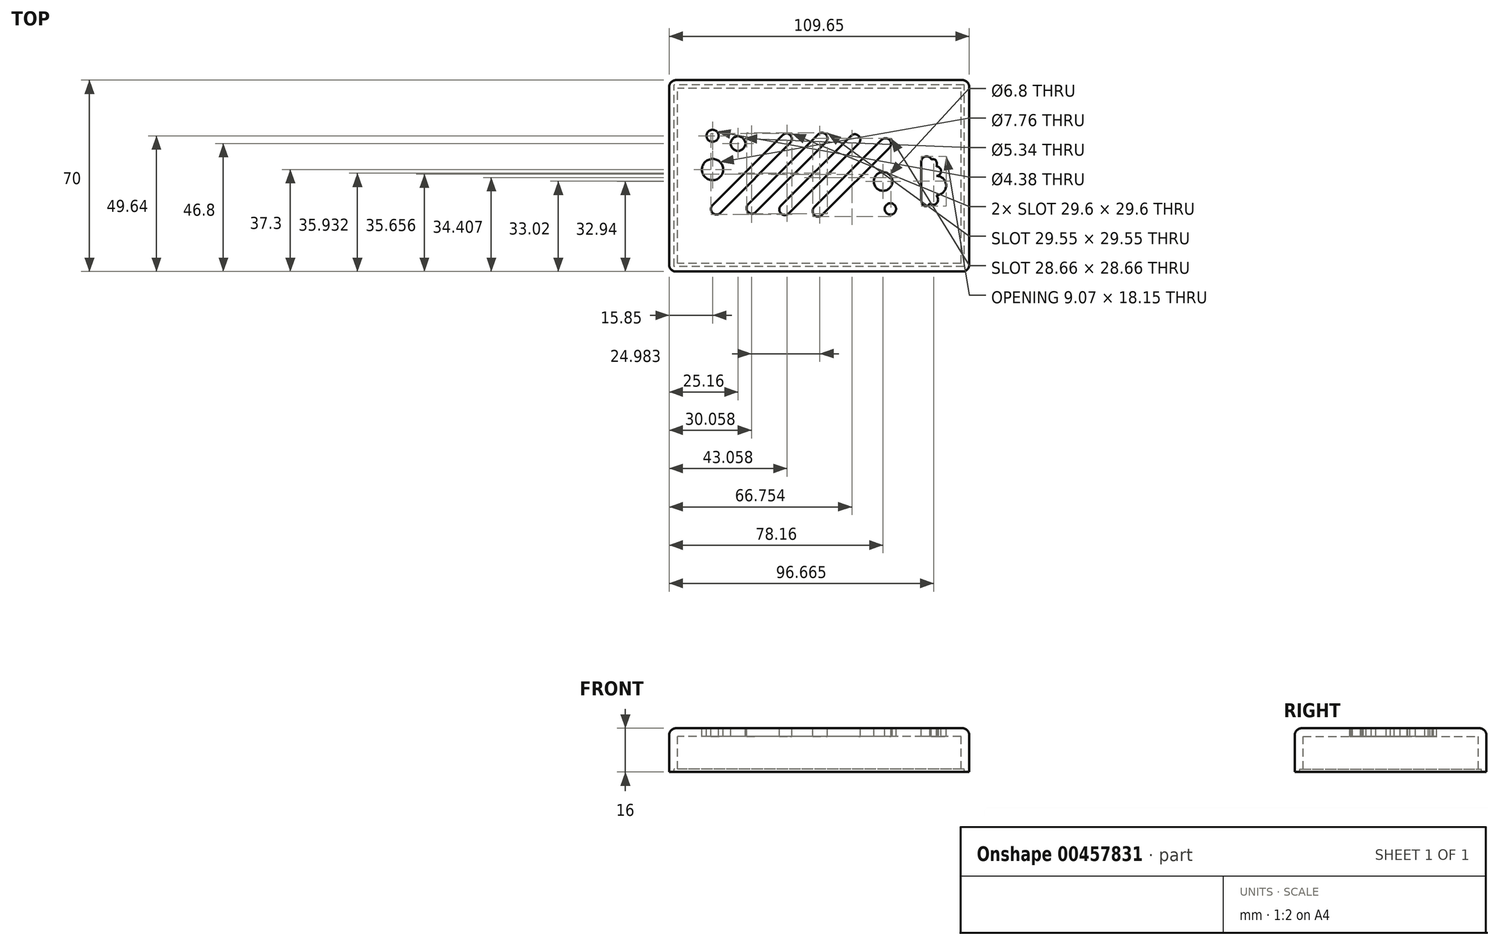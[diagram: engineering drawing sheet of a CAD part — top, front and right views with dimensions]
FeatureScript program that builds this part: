
annotation { "Feature Type Name" : "Feature", "Feature Type Description" : "" }
export const myFeature = defineFeature(function(context is Context, id is Id, definition is map)
    precondition{}
    {
        {
            var Q0;
            Q0=qCreatedBy(makeId("Top.planeOp"),FACE);
            var sketch = newSketch(context, id + "F0", { "sketchPlane" : qUnion([Q0])});
            skLineSegment(sketch, "E0.0", {"start": v(57.26, 37.06) * mm, "end": v(51.26, 37.06) * mm});
            skLineSegment(sketch, "E0.1", {"start": v(57.26, -32.94) * mm, "end": v(57.26, 37.06) * mm});
            skLineSegment(sketch, "E0.2", {"start": v(57.26, -32.94) * mm, "end": v(-24.39, -32.94) * mm});
            skLineSegment(sketch, "E0.3", {"start": v(-52.39, -32.94) * mm, "end": v(-52.39, 37.06) * mm});
            skLineSegment(sketch, "E1", {"start": v(-24.39, -32.94) * mm, "end": v(-46.39, -32.94) * mm});
            skLineSegment(sketch, "E2", {"start": v(-46.39, -32.94) * mm, "end": v(-52.39, -32.94) * mm});
            skLineSegment(sketch, "E3", {"start": v(51.26, 37.06) * mm, "end": v(29.26, 37.06) * mm});
            skLineSegment(sketch, "E4", {"start": v(29.26, 37.06) * mm, "end": v(-52.39, 37.06) * mm});
            skSolve(sketch);
        }
        {
            var Q0;
            Q0=makeQuery(id+"F0.imprint","IMPRINT",FACE,{"disambiguationData":[TD([[makeQuery(id+"F0.imprint","IMPRINT",EDGE,{"derivedFrom":sQuery(id+"F0.wireOp",EDGE,"E0.0")}),1.0]])]});
            extrude(context, id + "F1", {"entities" : qUnion([Q0]), "oppositeDirection" : true, "depth" : 15 * mm});
        }
        {
            var Q0;
            Q0=makeQuery(id+"F1.opExtrude","CAP_FACE",FACE,{"disambiguationData":[OSD([sQuery(id+"F0.wireOp",EDGE,"E0.0"),sQuery(id+"F0.wireOp",EDGE,"E0.1"),sQuery(id+"F0.wireOp",EDGE,"E0.2"),sQuery(id+"F0.wireOp",EDGE,"E0.3"),sQuery(id+"F0.wireOp",EDGE,"E1"),sQuery(id+"F0.wireOp",EDGE,"E2"),sQuery(id+"F0.wireOp",EDGE,"E3"),sQuery(id+"F0.wireOp",EDGE,"E4")])],"isStart":false});
            shell(context, id + "F2", {"entities" : qUnion([Q0]), "thickness" : 3 * mm});
        }
        {
            var Q0;
            Q0=makeQuery(id+"F1.opExtrude","SWEPT_EDGE",EDGE,{"disambiguationData":[OSD([sQuery(id+"F0.wireOp",EDGE,"E0.1"),sQuery(id+"F0.wireOp",EDGE,"E0.2")])]});
            var Q1;
            Q1=makeQuery(id+"F1.opExtrude","SWEPT_EDGE",EDGE,{"disambiguationData":[OSD([sQuery(id+"F0.wireOp",EDGE,"E0.0"),sQuery(id+"F0.wireOp",EDGE,"E0.1")])]});
            var Q2;
            Q2=makeQuery(id+"F1.opExtrude","SWEPT_EDGE",EDGE,{"disambiguationData":[OSD([sQuery(id+"F0.wireOp",EDGE,"E0.3"),sQuery(id+"F0.wireOp",EDGE,"E2")])]});
            var Q3;
            Q3=makeQuery(id+"F1.opExtrude","SWEPT_EDGE",EDGE,{"disambiguationData":[OSD([sQuery(id+"F0.wireOp",EDGE,"E0.3"),sQuery(id+"F0.wireOp",EDGE,"E4")])]});
            var Q4;
            Q4=makeQuery(id+"F1.opExtrude","CAP_EDGE",EDGE,{"disambiguationData":[OSD([sQuery(id+"F0.wireOp",EDGE,"E0.3")])],"isStart":true});
            var Q5;
            Q5=makeQuery(id+"F1.opExtrude","CAP_EDGE",EDGE,{"disambiguationData":[OSD([sQuery(id+"F0.wireOp",EDGE,"E0.2"),sQuery(id+"F0.wireOp",EDGE,"E1"),sQuery(id+"F0.wireOp",EDGE,"E2")])],"isStart":true});
            var Q6;
            Q6=makeQuery(id+"F1.opExtrude","CAP_EDGE",EDGE,{"disambiguationData":[OSD([sQuery(id+"F0.wireOp",EDGE,"E0.0"),sQuery(id+"F0.wireOp",EDGE,"E3"),sQuery(id+"F0.wireOp",EDGE,"E4")])],"isStart":true});
            var Q7;
            Q7=makeQuery(id+"F1.opExtrude","CAP_EDGE",EDGE,{"disambiguationData":[OSD([sQuery(id+"F0.wireOp",EDGE,"E0.1")])],"isStart":true});
            fillet(context, id + "F3", {"entities" : qUnion([Q0, Q1, Q2, Q3, Q4, Q5, Q6, Q7]), "radius" : 2.5 * mm, "tangentPropagation" : true, "allowEdgeOverflow" : false});
        }
        {
            var Q0;
            Q0=qCreatedBy(makeId("Top.planeOp"),FACE);
            var sketch = newSketch(context, id + "F4", { "sketchPlane" : qUnion([Q0])});
            skLineSegment(sketch, "E5.top", {"start": v(-36.54, -8.66) * mm, "end": v(-36.54, -8.66) * mm});
            skLineSegment(sketch, "E5.left", {"start": v(-10.95, 16.93) * mm, "end": v(-36.54, -8.66) * mm});
            skLineSegment(sketch, "E5.right", {"start": v(-8.12, 14.1) * mm, "end": v(-33.71, -11.5) * mm});
            skArc(sketch, "E6", {"start": v(-8.12, 14.1) * mm, "mid": v(-8.12, 16.93) * mm, "end": v(-10.95, 16.93) * mm});
            skArc(sketch, "E7", {"start": v(-36.54, -8.66) * mm, "mid": v(-36.54, -11.5) * mm, "end": v(-33.71, -11.5) * mm});
            skLineSegment(sketch, "E8.left", {"start": v(2.03, 17.18) * mm, "end": v(-23.52, -8.37) * mm});
            skLineSegment(sketch, "E8.right", {"start": v(4.85, 14.35) * mm, "end": v(-20.7, -11.2) * mm});
            skArc(sketch, "E9", {"start": v(4.85, 14.35) * mm, "mid": v(4.86, 17.18) * mm, "end": v(2.03, 17.18) * mm});
            skArc(sketch, "E10", {"start": v(-23.52, -8.37) * mm, "mid": v(-23.52, -11.2) * mm, "end": v(-20.7, -11.2) * mm});
            skLineSegment(sketch, "E11.left", {"start": v(14.03, 16.7) * mm, "end": v(-11.56, -8.9) * mm});
            skLineSegment(sketch, "E11.right", {"start": v(16.86, 13.86) * mm, "end": v(-8.73, -11.73) * mm});
            skArc(sketch, "E12", {"start": v(16.86, 13.86) * mm, "mid": v(16.86, 16.7) * mm, "end": v(14.03, 16.7) * mm});
            skArc(sketch, "E13", {"start": v(-11.56, -8.9) * mm, "mid": v(-11.56, -11.73) * mm, "end": v(-8.73, -11.73) * mm});
            skLineSegment(sketch, "E14.left", {"start": v(25.28, 15.21) * mm, "end": v(0.62, -9.45) * mm});
            skLineSegment(sketch, "E14.right", {"start": v(28.11, 12.38) * mm, "end": v(3.44, -12.28) * mm});
            skArc(sketch, "E15", {"start": v(28.11, 12.38) * mm, "mid": v(28.11, 15.21) * mm, "end": v(25.28, 15.21) * mm});
            skArc(sketch, "E16", {"start": v(0.62, -9.45) * mm, "mid": v(0.62, -12.28) * mm, "end": v(3.44, -12.28) * mm});
            skPoint(sketch, "E17.orphan", {"position": v(-8.73, 13.5) * mm});
            skSolve(sketch);
        }
        {
            var Q0;
            Q0=makeQuery(id+"F4.imprint","IMPRINT",FACE,{"disambiguationData":[TD([[makeQuery(id+"F4.imprint","IMPRINT",EDGE,{"derivedFrom":sQuery(id+"F4.wireOp",EDGE,"E14.left")}),1.0]])]});
            extrude(context, id + "F5", {"entities" : qUnion([Q0]), "operationType" : NewBodyOperationType.REMOVE, "oppositeDirection" : true, "depth" : 3 * mm});
        }
        {
            var Q0;
            {var subQ0=sQuery(id+"F4.wireOp",EDGE,"E8.left");Q0=makeQuery(id+"F4.imprint","IMPRINT",FACE,{"disambiguationData":[TD([[makeQuery(id+"F4.imprint","IMPRINT",EDGE,{"derivedFrom":subQ0}),1.0]])]});}
            extrude(context, id + "F6", {"entities" : qUnion([Q0]), "operationType" : NewBodyOperationType.REMOVE, "oppositeDirection" : true, "depth" : 3 * mm});
        }
        {
            var Q0;
            Q0=makeQuery(id+"F4.imprint","IMPRINT",FACE,{"disambiguationData":[TD([[makeQuery(id+"F4.imprint","IMPRINT",EDGE,{"derivedFrom":sQuery(id+"F4.wireOp",EDGE,"E11.left")}),1.0]])]});
            extrude(context, id + "F7", {"entities" : qUnion([Q0]), "operationType" : NewBodyOperationType.REMOVE, "oppositeDirection" : true, "depth" : 3 * mm});
        }
        {
            var Q0;
            Q0=makeQuery(id+"F4.imprint","IMPRINT",FACE,{"disambiguationData":[TD([[makeQuery(id+"F4.imprint","IMPRINT",EDGE,{"derivedFrom":sQuery(id+"F4.wireOp",EDGE,"E5.left")}),1.0]])]});
            extrude(context, id + "F8", {"entities" : qUnion([Q0]), "operationType" : NewBodyOperationType.REMOVE, "oppositeDirection" : true, "depth" : 3 * mm});
        }
        {
            var Q0;
            Q0=makeQuery(id+"F1.opExtrude","CAP_FACE",FACE,{"disambiguationData":[OSD([sQuery(id+"F0.wireOp",EDGE,"E0.0"),sQuery(id+"F0.wireOp",EDGE,"E0.1"),sQuery(id+"F0.wireOp",EDGE,"E0.2"),sQuery(id+"F0.wireOp",EDGE,"E0.3"),sQuery(id+"F0.wireOp",EDGE,"E1"),sQuery(id+"F0.wireOp",EDGE,"E2"),sQuery(id+"F0.wireOp",EDGE,"E3"),sQuery(id+"F0.wireOp",EDGE,"E4")])],"isStart":true});
            var sketch = newSketch(context, id + "F9", { "sketchPlane" : qUnion([Q0])});
            skCircle(sketch, "E18", {"center": v(25.77, 0) * mm, "radius": 3.4 * mm});
            skCircle(sketch, "E19", {"center": v(28.45, -10.04) * mm, "radius": 2.08 * mm});
            skCircle(sketch, "E20", {"center": v(-36.54, 16.7) * mm, "radius": 2.19 * mm});
            skCircle(sketch, "E21", {"center": v(-27.23, 13.86) * mm, "radius": 2.67 * mm});
            skCircle(sketch, "E22", {"center": v(-36.54, 4.36) * mm, "radius": 3.88 * mm});
            skSolve(sketch);
        }
        {
            var Q0;
            Q0=makeQuery(id+"F9.imprint","IMPRINT",FACE,{"disambiguationData":[TD([[makeQuery(id+"F9.imprint","IMPRINT",EDGE,{"derivedFrom":sQuery(id+"F9.wireOp",EDGE,"E18")}),1.0]])]});
            var Q1;
            Q1=makeQuery(id+"F9.imprint","IMPRINT",FACE,{"disambiguationData":[TD([[makeQuery(id+"F9.imprint","IMPRINT",EDGE,{"derivedFrom":sQuery(id+"F9.wireOp",EDGE,"E19")}),1.0]])]});
            var Q2;
            Q2=makeQuery(id+"F9.imprint","IMPRINT",FACE,{"disambiguationData":[TD([[makeQuery(id+"F9.imprint","IMPRINT",EDGE,{"derivedFrom":sQuery(id+"F9.wireOp",EDGE,"E22")}),1.0]])]});
            var Q3;
            Q3=makeQuery(id+"F9.imprint","IMPRINT",FACE,{"disambiguationData":[TD([[makeQuery(id+"F9.imprint","IMPRINT",EDGE,{"derivedFrom":sQuery(id+"F9.wireOp",EDGE,"E21")}),1.0]])]});
            var Q4;
            Q4=makeQuery(id+"F9.imprint","IMPRINT",FACE,{"disambiguationData":[TD([[makeQuery(id+"F9.imprint","IMPRINT",EDGE,{"derivedFrom":sQuery(id+"F9.wireOp",EDGE,"E20")}),1.0]])]});
            extrude(context, id + "F10", {"entities" : qUnion([Q0, Q1, Q2, Q3, Q4]), "operationType" : NewBodyOperationType.REMOVE, "oppositeDirection" : true, "depth" : 3 * mm});
        }
        {
            var Q0;
            Q0=makeQuery(id+"F1.opExtrude","CAP_FACE",FACE,{"disambiguationData":[OSD([sQuery(id+"F0.wireOp",EDGE,"E0.0"),sQuery(id+"F0.wireOp",EDGE,"E0.1"),sQuery(id+"F0.wireOp",EDGE,"E0.2"),sQuery(id+"F0.wireOp",EDGE,"E0.3"),sQuery(id+"F0.wireOp",EDGE,"E1"),sQuery(id+"F0.wireOp",EDGE,"E2"),sQuery(id+"F0.wireOp",EDGE,"E3"),sQuery(id+"F0.wireOp",EDGE,"E4")])],"isStart":false});
            var sketch = newSketch(context, id + "F11", { "sketchPlane" : qUnion([Q0])});
            skLineSegment(sketch, "E23.0", {"start": v(-50.59, 31.14) * mm, "end": v(-50.59, -35.26) * mm});
            skLineSegment(sketch, "E23.1", {"start": v(55.46, 31.14) * mm, "end": v(-50.59, 31.14) * mm});
            skLineSegment(sketch, "E23.2", {"start": v(55.46, 31.14) * mm, "end": v(55.46, -35.26) * mm});
            skLineSegment(sketch, "E23.3", {"start": v(55.46, -35.26) * mm, "end": v(-50.59, -35.26) * mm});
            skSolve(sketch);
        }
        {
            var Q0;
            Q0=makeQuery(id+"F11.imprint","IMPRINT",FACE,{"disambiguationData":[TD([[makeQuery(id+"F11.imprint","IMPRINT",EDGE,{"derivedFrom":sQuery(id+"F11.wireOp",EDGE,"E23.0")}),-1.0]])]});
            extrude(context, id + "F12", {"entities" : qUnion([Q0]), "operationType" : NewBodyOperationType.ADD, "depth" : 1 * mm});
        }
        {
            var Q0;
            Q0=qCreatedBy(makeId("Top.planeOp"),FACE);
            var sketch = newSketch(context, id + "F13", { "sketchPlane" : qUnion([Q0])});
            skLineSegment(sketch, "E24.bottom", {"start": v(41.25, -9) * mm, "end": v(41.56, -9) * mm, "construction": true});
            skArc(sketch, "E25", {"start": v(39.74, 7.22) * mm, "mid": v(41.2, 9.1) * mm, "end": v(43.38, 8.15) * mm});
            skFitSpline(sketch, "E26", {"points": [v(43.38, 8.15) * mm, v(45.28, 5.49) * mm], "startDerivative": vector(6.59, 1.21) * mm, "endDerivative": vector(-1.3, -1.6) * mm});
            skLineSegment(sketch, "E27.right", {"start": v(39.74, 7.22) * mm, "end": v(39.74, -6.84) * mm});
            skArc(sketch, "E28", {"start": v(45.28, 5.49) * mm, "mid": v(47, 3.77) * mm, "end": v(45.28, 2.04) * mm});
            skArc(sketch, "E29", {"start": v(45.28, -5.03) * mm, "mid": v(48.81, -1.5) * mm, "end": v(45.28, 2.04) * mm});
            skFitSpline(sketch, "E30", {"points": [v(45.28, -5.03) * mm, v(45.86, -6.36) * mm, v(45.57, -7.72) * mm, v(44.63, -8.45) * mm, v(43.5, -8.4) * mm, v(42.82, -7.98) * mm], "startDerivative": vector(3.56, -5.65) * mm, "endDerivative": vector(-2.1, 3.76) * mm});
            skFitSpline(sketch, "E31", {"points": [v(42.82, -7.98) * mm, v(42.2, -8.78) * mm, v(41.25, -9) * mm, v(40.22, -8.52) * mm, v(39.74, -6.84) * mm], "startDerivative": vector(-2.28, -4) * mm, "endDerivative": vector(-0.28, 6.78) * mm});
            skArc(sketch, "E32", {"start": v(46.35, -7.54) * mm, "mid": v(45.38, -8.75) * mm, "end": v(43.85, -9.03) * mm});
            skArc(sketch, "E33", {"start": v(47.51, -7.93) * mm, "mid": v(45.96, -9.83) * mm, "end": v(43.54, -10.22) * mm});
            skArc(sketch, "E34.0", {"start": v(46.92, -7.73) * mm, "mid": v(45.69, -9.27) * mm, "end": v(43.75, -9.63) * mm});
            skArc(sketch, "E35.0", {"start": v(48.08, -8.12) * mm, "mid": v(46.26, -10.35) * mm, "end": v(43.42, -10.81) * mm});
            skArc(sketch, "E36", {"start": v(46.9, -7.76) * mm, "mid": v(46.73, -7.36) * mm, "end": v(46.34, -7.56) * mm});
            skPoint(sketch, "E36.third.point", {"position": v(46.8, -7.4) * mm});
            skArc(sketch, "E37", {"start": v(48.07, -8.15) * mm, "mid": v(47.9, -7.75) * mm, "end": v(47.5, -7.95) * mm});
            skPoint(sketch, "E37.third.point", {"position": v(47.92, -7.76) * mm});
            skArc(sketch, "E38", {"start": v(43.92, -9.05) * mm, "mid": v(43.54, -9.3) * mm, "end": v(43.84, -9.64) * mm});
            skPoint(sketch, "E38.third.point", {"position": v(43.54, -9.34) * mm});
            skArc(sketch, "E39", {"start": v(43.55, -10.23) * mm, "mid": v(43.19, -10.46) * mm, "end": v(43.43, -10.81) * mm});
            skPoint(sketch, "E39.third.point", {"position": v(43.19, -10.57) * mm});
            skSolve(sketch);
        }
        {
            var Q0;
            Q0 = qSketchRegion(id + "F13", true);
            extrude(context, id + "F14", {"entities" : qUnion([Q0]), "operationType" : NewBodyOperationType.REMOVE, "oppositeDirection" : true, "depth" : 3 * mm});
        }
    });
